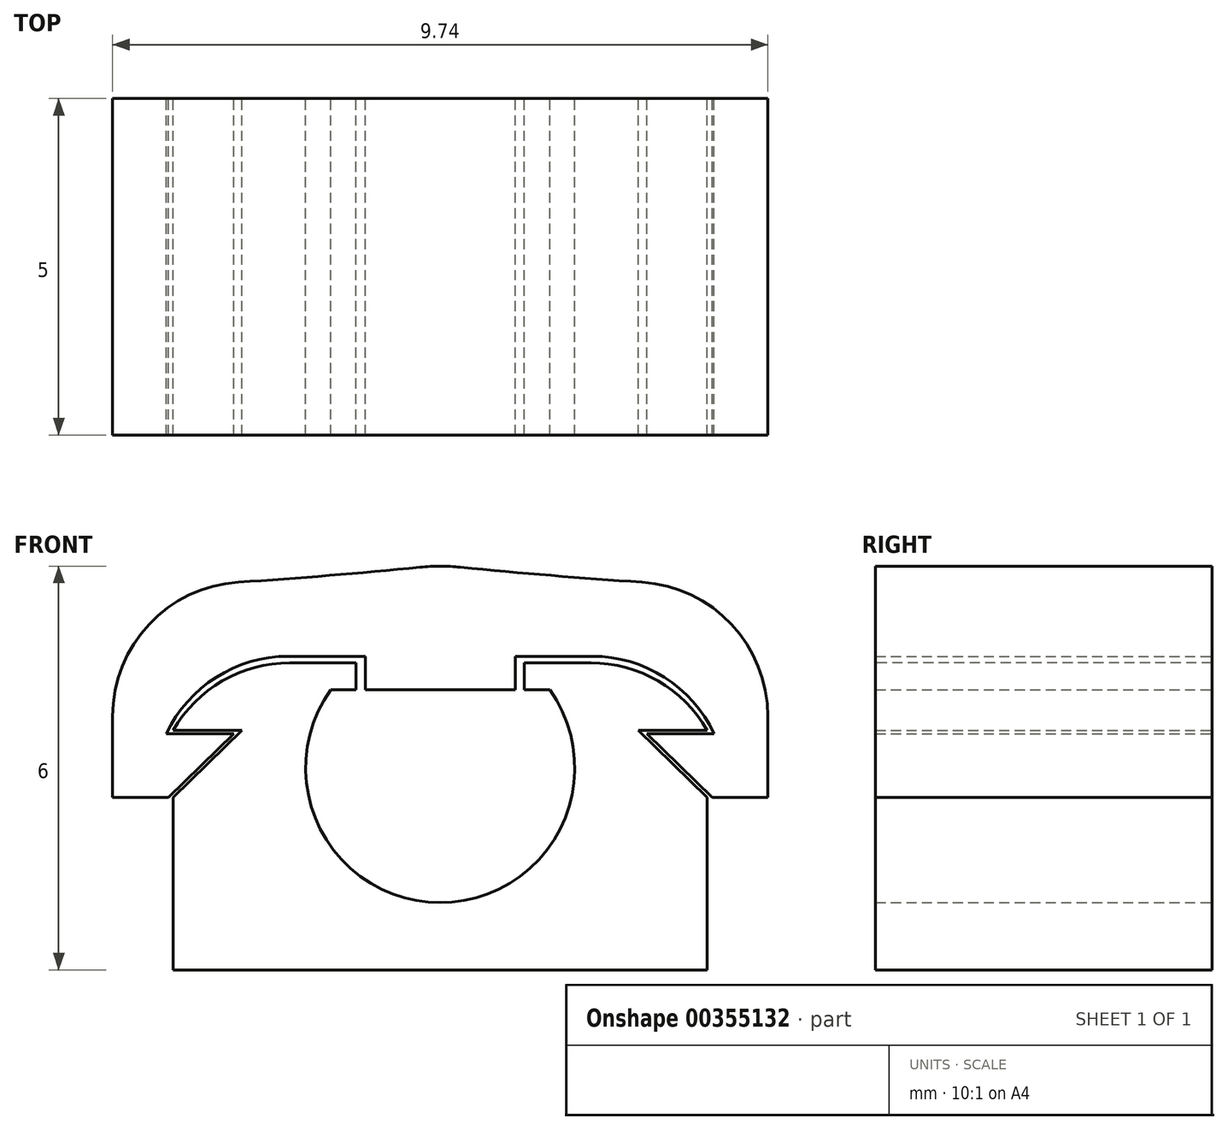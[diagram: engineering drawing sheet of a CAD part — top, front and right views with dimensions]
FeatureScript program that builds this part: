
annotation { "Feature Type Name" : "Feature", "Feature Type Description" : "" }
export const myFeature = defineFeature(function(context is Context, id is Id, definition is map)
    precondition{}
    {
        {
            var Q0;
            Q0=qCreatedBy(makeId("Front.planeOp"),FACE);
            var sketch = newSketch(context, id + "F0", { "sketchPlane" : qUnion([Q0])});
            skCircle(sketch, "E0", {"center": v(0, 0) * mm, "radius": 2 * mm});
            skLineSegment(sketch, "E1", {"start": v(0, 4.87) * mm, "end": v(0, -3.44) * mm, "construction": true});
            skLineSegment(sketch, "E2.0", {"start": v(3.97, 1.56) * mm, "end": v(3.97, -3) * mm});
            skLineSegment(sketch, "E2.1", {"start": v(3.97, -3) * mm, "end": v(0, -3) * mm});
            skLineSegment(sketch, "E2.2", {"start": v(-3.97, -3) * mm, "end": v(0, -3) * mm});
            skLineSegment(sketch, "E2.3", {"start": v(-3.97, 1.56) * mm, "end": v(-3.97, -3) * mm});
            skLineSegment(sketch, "E3", {"start": v(-3.97, 1.56) * mm, "end": v(-1.25, 1.56) * mm});
            skLineSegment(sketch, "E4", {"start": v(1.25, 1.56) * mm, "end": v(3.97, 1.56) * mm});
            skCircle(sketch, "E5", {"center": v(0, 0) * mm, "radius": 3 * mm});
            skLineSegment(sketch, "E6", {"start": v(-3.97, 0.56) * mm, "end": v(-2.95, 0.56) * mm});
            skLineSegment(sketch, "E7", {"start": v(-2.95, 0.56) * mm, "end": v(-3.97, -0.44) * mm});
            skLineSegment(sketch, "E8.MirrorCS", {"start": v(2.95, 0.56) * mm, "end": v(3.97, -0.44) * mm});
            skLineSegment(sketch, "E9.MirrorCS", {"start": v(3.97, 0.56) * mm, "end": v(2.95, 0.56) * mm});
            skLineSegment(sketch, "E10", {"start": v(-4.07, 0.51) * mm, "end": v(-3.07, 0.51) * mm});
            skLineSegment(sketch, "E11", {"start": v(-3.07, 0.51) * mm, "end": v(-4.04, -0.44) * mm});
            skLineSegment(sketch, "E12", {"start": v(-1.16, 2.77) * mm, "end": v(-4.87, 2.77) * mm});
            skLineSegment(sketch, "E13", {"start": v(-4.87, 2.77) * mm, "end": v(-4.87, -0.44) * mm});
            skLineSegment(sketch, "E14", {"start": v(-4.87, -0.44) * mm, "end": v(-4.04, -0.44) * mm});
            skLineSegment(sketch, "E15", {"start": v(-4.07, 1.66) * mm, "end": v(-4.07, 0.51) * mm});
            skLineSegment(sketch, "E16", {"start": v(-4.07, 1.66) * mm, "end": v(-1.11, 1.66) * mm});
            skLineSegment(sketch, "E17.MirrorCS", {"start": v(4.07, 0.51) * mm, "end": v(3.07, 0.51) * mm});
            skLineSegment(sketch, "E18.MirrorCS", {"start": v(3.07, 0.51) * mm, "end": v(4.04, -0.44) * mm});
            skLineSegment(sketch, "E19.MirrorCS", {"start": v(4.87, -0.44) * mm, "end": v(4.04, -0.44) * mm});
            skLineSegment(sketch, "E20.MirrorCS", {"start": v(4.07, 1.66) * mm, "end": v(4.07, 0.51) * mm});
            skLineSegment(sketch, "E21.MirrorCS", {"start": v(4.87, 2.77) * mm, "end": v(4.87, -0.44) * mm});
            skLineSegment(sketch, "E22.MirrorCS", {"start": v(1.16, 2.77) * mm, "end": v(4.87, 2.77) * mm});
            skLineSegment(sketch, "E23.MirrorCS", {"start": v(4.07, 1.66) * mm, "end": v(1.11, 1.66) * mm});
            skLineSegment(sketch, "E24", {"start": v(1.11, 1.66) * mm, "end": v(1.11, 1.16) * mm});
            skLineSegment(sketch, "E25", {"start": v(1.11, 1.16) * mm, "end": v(0, 1.16) * mm});
            skLineSegment(sketch, "E26.MirrorCS", {"start": v(-1.11, 1.16) * mm, "end": v(0, 1.16) * mm});
            skLineSegment(sketch, "E27.MirrorCS", {"start": v(-1.11, 1.66) * mm, "end": v(-1.11, 1.16) * mm});
            skLineSegment(sketch, "E28", {"start": v(-1.25, 1.56) * mm, "end": v(-1.25, 1.16) * mm});
            skLineSegment(sketch, "E29", {"start": v(-1.25, 1.16) * mm, "end": v(-1.63, 1.16) * mm});
            skLineSegment(sketch, "E30.MirrorCS", {"start": v(1.25, 1.56) * mm, "end": v(1.25, 1.16) * mm});
            skLineSegment(sketch, "E31.MirrorCS", {"start": v(1.25, 1.16) * mm, "end": v(1.63, 1.16) * mm});
            skSolve(sketch);
        }
        {
            var Q0;
            {var subQ0=sQuery(id+"F0.wireOp",EDGE,"E3");var subQ1=sQuery(id+"F0.wireOp",EDGE,"E0");var subQ2=makeQuery(id+"F0.imprint","INTERSECT",VERTEX,{"derivedFrom":[subQ1,subQ0]});Q0=makeQuery(id+"F0.imprint","IMPRINT",FACE,{"disambiguationData":[TD([[makeQuery(id+"F0.imprint","IMPRINT",EDGE,{"disambiguationData":[TD([[subQ2,-1.0]])],"derivedFrom":subQ1}),-1.0]])]});}
            var Q1;
            {var subQ0=sQuery(id+"F0.wireOp",EDGE,"E2.2");Q1=makeQuery(id+"F0.imprint","IMPRINT",FACE,{"disambiguationData":[TD([[makeQuery(id+"F0.imprint","IMPRINT",EDGE,{"derivedFrom":subQ0}),1.0]])]});}
            var Q2;
            {var subQ3=sQuery(id+"F0.wireOp",EDGE,"E6");Q2=makeQuery(id+"F0.imprint","IMPRINT",FACE,{"disambiguationData":[TD([[makeQuery(id+"F0.imprint","IMPRINT",EDGE,{"derivedFrom":subQ3}),1.0]])]});}
            var Q3;
            {var subQ3=sQuery(id+"F0.wireOp",EDGE,"E9.MirrorCS");Q3=makeQuery(id+"F0.imprint","IMPRINT",FACE,{"disambiguationData":[TD([[makeQuery(id+"F0.imprint","IMPRINT",EDGE,{"derivedFrom":subQ3}),-1.0]])]});}
            var Q4;
            {var subQ0=sQuery(id+"F0.wireOp",EDGE,"E2.1");Q4=makeQuery(id+"F0.imprint","IMPRINT",FACE,{"disambiguationData":[TD([[makeQuery(id+"F0.imprint","IMPRINT",EDGE,{"derivedFrom":subQ0}),-1.0]])]});}
            var Q5;
            {var subQ4=sQuery(id+"F0.wireOp",EDGE,"E12");Q5=makeQuery(id+"F0.imprint","IMPRINT",FACE,{"disambiguationData":[TD([[makeQuery(id+"F0.imprint","IMPRINT",EDGE,{"derivedFrom":subQ4}),1.0]])]});}
            var Q6;
            {var subQ0=sQuery(id+"F0.wireOp",EDGE,"E11");var subQ1=sQuery(id+"F0.wireOp",EDGE,"E2.3");var subQ2=makeQuery(id+"F0.imprint","INTERSECT",VERTEX,{"derivedFrom":[subQ1,subQ0]});Q6=makeQuery(id+"F0.imprint","IMPRINT",FACE,{"disambiguationData":[TD([[makeQuery(id+"F0.imprint","IMPRINT",EDGE,{"disambiguationData":[TD([[subQ2,1.0]])],"derivedFrom":subQ1}),1.0]])]});}
            var Q7;
            {var subQ2=sQuery(id+"F0.wireOp",EDGE,"E16");var subQ5=sQuery(id+"F0.wireOp",EDGE,"E0");var subQ6=makeQuery(id+"F0.imprint","INTERSECT",VERTEX,{"derivedFrom":[subQ5,subQ2]});Q7=makeQuery(id+"F0.imprint","IMPRINT",FACE,{"disambiguationData":[TD([[makeQuery(id+"F0.imprint","IMPRINT",EDGE,{"disambiguationData":[TD([[subQ6,1.0]])],"derivedFrom":subQ5}),-1.0]])]});}
            var Q8;
            {var subQ8=sQuery(id+"F0.wireOp",EDGE,"E19.MirrorCS");Q8=makeQuery(id+"F0.imprint","IMPRINT",FACE,{"disambiguationData":[TD([[makeQuery(id+"F0.imprint","IMPRINT",EDGE,{"derivedFrom":subQ8}),-1.0]])]});}
            var Q9;
            {var subQ0=sQuery(id+"F0.wireOp",EDGE,"E18.MirrorCS");var subQ1=sQuery(id+"F0.wireOp",EDGE,"E2.0");var subQ2=makeQuery(id+"F0.imprint","INTERSECT",VERTEX,{"derivedFrom":[subQ1,subQ0]});Q9=makeQuery(id+"F0.imprint","IMPRINT",FACE,{"disambiguationData":[TD([[makeQuery(id+"F0.imprint","IMPRINT",EDGE,{"disambiguationData":[TD([[subQ2,1.0]])],"derivedFrom":subQ1}),-1.0]])]});}
            var Q10;
            {var subQ0=sQuery(id+"F0.wireOp",EDGE,"q89pCRjA-3Hjy-f9lH-HpBs-NVLH9aL46BUT");Q10=makeQuery(id+"F0.imprint","IMPRINT",FACE,{"disambiguationData":[TD([[makeQuery(id+"F0.imprint","IMPRINT",EDGE,{"derivedFrom":subQ0}),1.0]])]});}
            var Q11;
            {var subQ0=sQuery(id+"F0.wireOp",EDGE,"E24");Q11=makeQuery(id+"F0.imprint","IMPRINT",FACE,{"disambiguationData":[TD([[makeQuery(id+"F0.imprint","IMPRINT",EDGE,{"derivedFrom":subQ0}),-1.0]])]});}
            var Q12;
            {var subQ0=sQuery(id+"F0.wireOp",EDGE,"E28");Q12=makeQuery(id+"F0.imprint","IMPRINT",FACE,{"disambiguationData":[TD([[makeQuery(id+"F0.imprint","IMPRINT",EDGE,{"derivedFrom":subQ0}),-1.0]])]});}
            var Q13;
            {var subQ0=sQuery(id+"F0.wireOp",EDGE,"E30.MirrorCS");Q13=makeQuery(id+"F0.imprint","IMPRINT",FACE,{"disambiguationData":[TD([[makeQuery(id+"F0.imprint","IMPRINT",EDGE,{"derivedFrom":subQ0}),1.0]])]});}
            extrude(context, id + "F1", {"entities" : qUnion([Q0, Q1, Q2, Q3, Q4, Q5, Q6, Q7, Q8, Q9, Q10, Q11, Q12, Q13]), "depth" : 5 * mm});
        }
        {
            var Q0;
            Q0=makeQuery(id+"F1.opExtrude","SWEPT_EDGE",EDGE,{"disambiguationData":[OSD([sQuery(id+"F0.wireOp",EDGE,"E12"),sQuery(id+"F0.wireOp",EDGE,"E13")])]});
            var Q1;
            Q1=makeQuery(id+"F1.opExtrude","SWEPT_EDGE",EDGE,{"disambiguationData":[OSD([sQuery(id+"F0.wireOp",EDGE,"E21.MirrorCS"),sQuery(id+"F0.wireOp",EDGE,"E22.MirrorCS")])]});
            var Q2;
            Q2=makeQuery(id+"F1.opExtrude","SWEPT_EDGE",EDGE,{"disambiguationData":[OSD([sQuery(id+"F0.wireOp",EDGE,"E2.3"),sQuery(id+"F0.wireOp",EDGE,"E3")])]});
            var Q3;
            Q3=makeQuery(id+"F1.opExtrude","SWEPT_EDGE",EDGE,{"disambiguationData":[OSD([sQuery(id+"F0.wireOp",EDGE,"E15"),sQuery(id+"F0.wireOp",EDGE,"E16")])]});
            var Q4;
            Q4=makeQuery(id+"F1.opExtrude","SWEPT_EDGE",EDGE,{"disambiguationData":[OSD([sQuery(id+"F0.wireOp",EDGE,"E2.0"),sQuery(id+"F0.wireOp",EDGE,"E4")])]});
            var Q5;
            Q5=makeQuery(id+"F1.opExtrude","SWEPT_EDGE",EDGE,{"disambiguationData":[OSD([sQuery(id+"F0.wireOp",EDGE,"E20.MirrorCS"),sQuery(id+"F0.wireOp",EDGE,"E23.MirrorCS")])]});
            fillet(context, id + "F2", {"entities" : qUnion([Q0, Q1, Q2, Q3, Q4, Q5]), "radius" : 2 * mm, "tangentPropagation" : true, "allowEdgeOverflow" : false});
        }
        {
            var Q0;
            Q0=makeQuery(id+"F1.opExtrude","SWEPT_EDGE",EDGE,{"disambiguationData":[OSD([sQuery(id+"F0.wireOp",EDGE,"E5"),sQuery(id+"F0.wireOp",EDGE,"E22.MirrorCS")])]});
            var Q1;
            Q1=makeQuery(id+"F1.opExtrude","SWEPT_EDGE",EDGE,{"disambiguationData":[OSD([sQuery(id+"F0.wireOp",EDGE,"E5"),sQuery(id+"F0.wireOp",EDGE,"E12")])]});
            fillet(context, id + "F3", {"entities" : qUnion([Q0, Q1]), "radius" : 77.45 * mm, "tangentPropagation" : true, "allowEdgeOverflow" : false});
        }
    });
